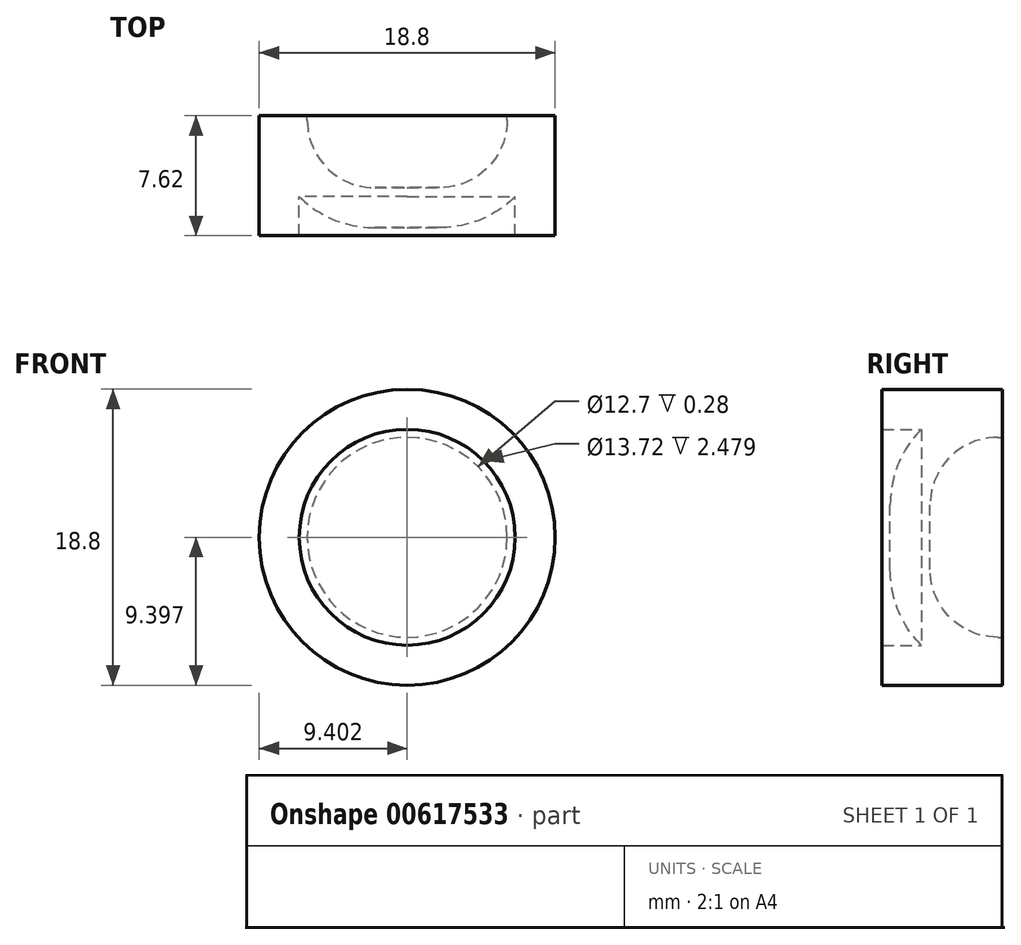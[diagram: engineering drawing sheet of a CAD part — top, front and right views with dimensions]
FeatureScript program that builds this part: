
annotation { "Feature Type Name" : "Feature", "Feature Type Description" : "" }
export const myFeature = defineFeature(function(context is Context, id is Id, definition is map)
    precondition{}
    {
        {
            var Q0;
            Q0=qCreatedBy(makeId("Front.planeOp"),FACE);
            var sketch = newSketch(context, id + "F0", { "sketchPlane" : qUnion([Q0])});
            skCircle(sketch, "E0", {"center": v(3.71, 24.07) * mm, "radius": 9.4 * mm});
            skSolve(sketch);
        }
        {
            var Q0;
            Q0=makeQuery(id+"F0.imprint","IMPRINT",FACE,{"disambiguationData":[TD([[makeQuery(id+"F0.imprint","IMPRINT",EDGE,{"derivedFrom":sQuery(id+"F0.wireOp",EDGE,"E0")}),1.0]])]});
            extrude(context, id + "F1", {"entities" : qUnion([Q0]), "depth" : 7.62 * mm, "offsetDistance" : 25.4 * mm});
        }
        {
            var Q0;
            Q0=makeQuery(id+"F1.opExtrude","CAP_FACE",FACE,{"disambiguationData":[OSD([sQuery(id+"F0.wireOp",EDGE,"E0")])],"isStart":true});
            shell(context, id + "F2", {"entities" : qUnion([Q0]), "thickness" : 3.05 * mm});
        }
        {
            var Q0;
            {var subQ0=sQuery(id+"F0.wireOp",EDGE,"E0");Q0=makeQuery(id+"F2.opShell","OFFSET_FACE",FACE,{"disambiguationData":[OSD([subQ0]),TDD([makeQuery(id+"F1.opExtrude","CAP_FACE",FACE,{"disambiguationData":[OSD([subQ0])],"isStart":false})])]});}
            fillet(context, id + "F3", {"entities" : qUnion([Q0]), "radius" : 4.3 * mm, "tangentPropagation" : true, "allowEdgeOverflow" : false});
        }
        {
            var Q0;
            Q0=makeQuery(id+"F1.opExtrude","CAP_FACE",FACE,{"disambiguationData":[OSD([sQuery(id+"F0.wireOp",EDGE,"E0")])],"isStart":false});
            shell(context, id + "F4", {"entities" : qUnion([Q0]), "thickness" : 2.54 * mm});
        }
    });
